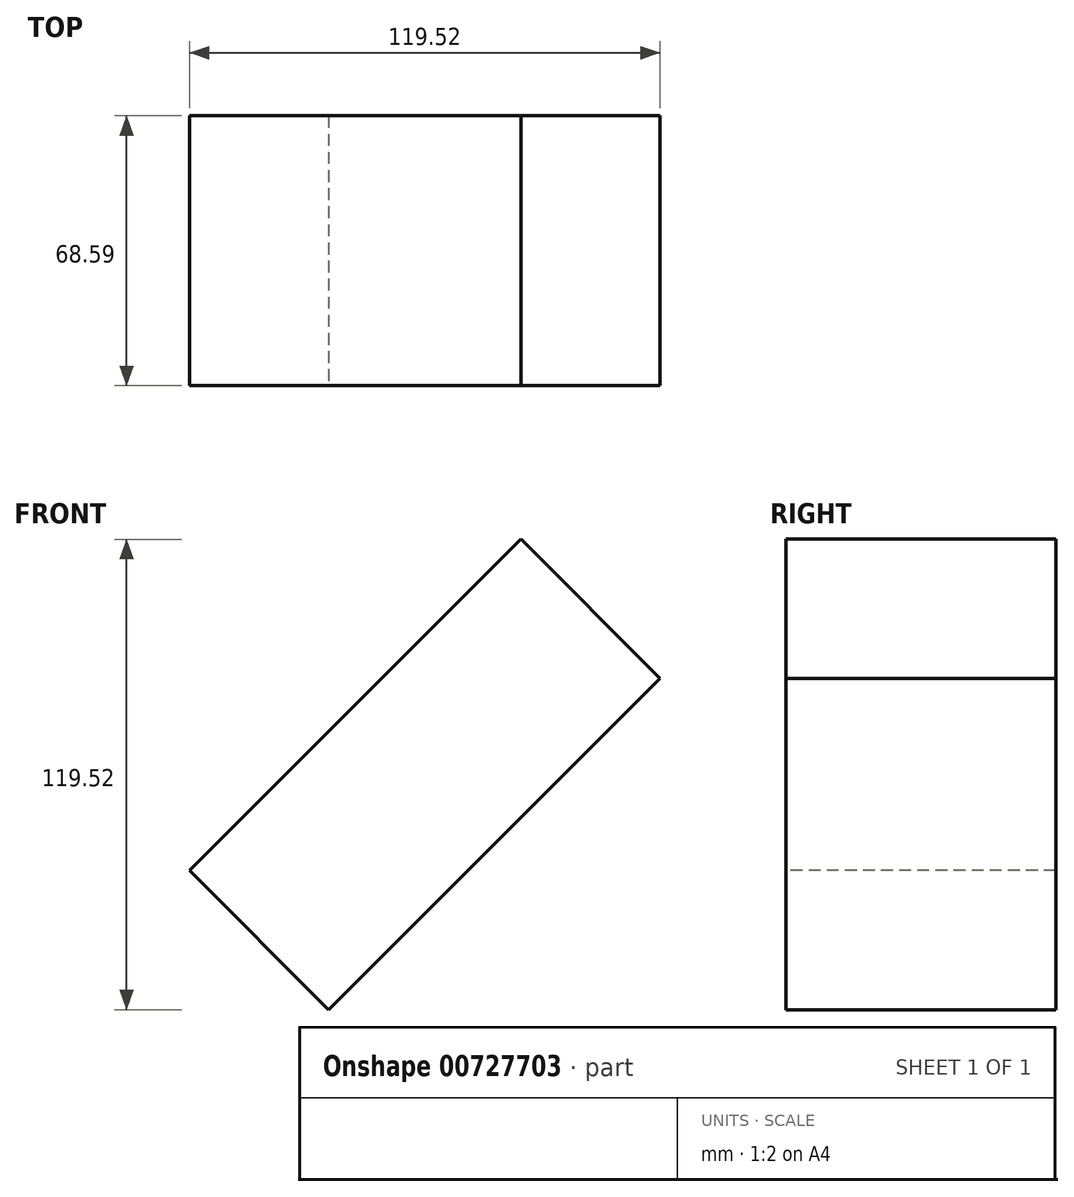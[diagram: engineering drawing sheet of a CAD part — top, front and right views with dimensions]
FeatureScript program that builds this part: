
annotation { "Feature Type Name" : "Feature", "Feature Type Description" : "" }
export const myFeature = defineFeature(function(context is Context, id is Id, definition is map)
    precondition{}
    {
        {
            var Q0;
            Q0=qCreatedBy(makeId("Top.planeOp"),FACE);
            var sketch = newSketch(context, id + "F0", { "sketchPlane" : qUnion([Q0])});
            skLineSegment(sketch, "E0.bottom", {"start": v(-61.06, 32.2) * mm, "end": v(57.97, 32.2) * mm});
            skLineSegment(sketch, "E0.top", {"start": v(-61.06, -36.38) * mm, "end": v(57.97, -36.38) * mm});
            skLineSegment(sketch, "E0.left", {"start": v(-61.06, 32.2) * mm, "end": v(-61.06, -36.38) * mm});
            skLineSegment(sketch, "E0.right", {"start": v(57.97, 32.2) * mm, "end": v(57.97, -36.38) * mm});
            skSolve(sketch);
        }
        {
            var Q0;
            Q0=makeQuery(id+"F0.imprint","IMPRINT",FACE,{"disambiguationData":[TD([[makeQuery(id+"F0.imprint","IMPRINT",EDGE,{"derivedFrom":sQuery(id+"F0.wireOp",EDGE,"E0.bottom")}),-1.0]])]});
            extrude(context, id + "F1", {"entities" : qUnion([Q0]), "depth" : 50 * mm, "offsetDistance" : 25 * mm});
        }
        {
            var Q0;
            Q0=makeQuery(id+"F1.opExtrude","SWEPT_BODY",BODY,{"disambiguationData":[OSD([sQuery(id+"F0.wireOp",EDGE,"E0.bottom"),sQuery(id+"F0.wireOp",EDGE,"E0.top"),sQuery(id+"F0.wireOp",EDGE,"E0.left"),sQuery(id+"F0.wireOp",EDGE,"E0.right")])]});
            var Q1;
            Q1=makeQuery(id+"F1.opExtrude","CAP_EDGE",EDGE,{"disambiguationData":[OSD([sQuery(id+"F0.wireOp",EDGE,"E0.left")])],"isStart":true});
            transform(context, id + "F2", {"entities" : qUnion([Q0]), "transformType" : TransformType.ROTATION, "transformAxis" : qUnion([Q1]), "angle" : 45 * degree, "makeCopy" : false});
        }
    });
